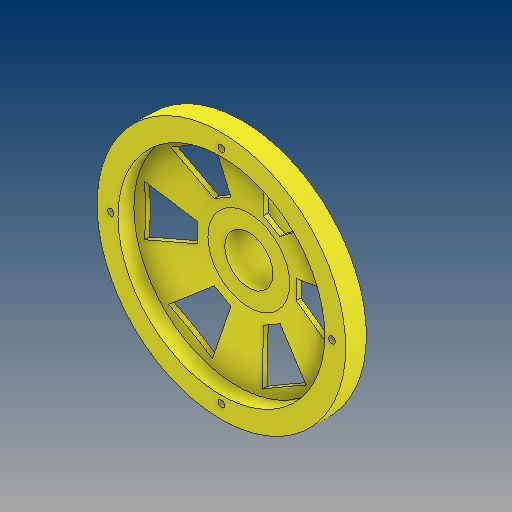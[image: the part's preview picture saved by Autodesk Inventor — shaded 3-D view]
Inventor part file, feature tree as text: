
AUTODESK INVENTOR PART (.ipt)
format: ipt  version: 2021 (Build 250183000, 183)  size: 367,616 bytes
history: native  units: in
note: dims shown in document units (in); Inventor stores cm internally (conversion verified against a paired STEP export)
features: sketch x10, thread x9, extrude x6, pattern_circular x5, revolve x4, plane x1
ambient origin geometry x8: Origin, YZ Plane, XZ Plane, XY Plane, X Axis, Y Axis, Z Axis, Center Point
bodies: Solid2 (feature_tree)
feature tree (35):
  plane  "Work Plane1"
  extrude  "Extrusion2"  Depth=3.0315in TaperAngle=0.0deg
  extrude  "Extrusion3"  Depth=3.937in
  revolve  "Revolution1"  Angle=90.0deg
  extrude  "Extrusion5"  Depth=2.3622in TaperAngle=360.0deg
  pattern_circular  "Circular Pattern2"  Count=14  [1 undecoded]
  extrude  "Extrusion9"  Depth=0.3937in TaperAngle=0.0deg
  extrude  "Extrusion10"  Depth=9.0551in
  pattern_circular  "Circular Pattern4"  Count=4 Angle=360.0deg
  sketch  "Sketch14"  dims[d43=0.9843in d44=0.0in d47=1.5748in d48=360.0deg d58=20.3543in d59=10.1772in d61=0.9843in d62=0.0in d63=0.9843in d64=0.0in]
  thread  "Thread5"  [1 undecoded]
  thread  "Thread6"  [1 undecoded]
  thread  "Thread7"  [1 undecoded]
  thread  "Thread8"  [1 undecoded]
  revolve  "Revolution4"  [1 undecoded]
  pattern_circular  "Circular Pattern5"  Count=4 Angle=360.0deg
  extrude  "Extrusion12"  Depth=0.3937in
  revolve  "Revolution5"  [1 undecoded]
  pattern_circular  "Circular Pattern6"  Angle=45.0deg  [1 undecoded]
  thread  "Thread9"  [1 undecoded]
  thread  "Thread10"  [1 undecoded]
  thread  "Thread11"  [1 undecoded]
  thread  "Thread12"  [1 undecoded]
  thread  "Thread13"  [1 undecoded]
  revolve  "Revolution6"  [1 undecoded]
  pattern_circular  "Circular Pattern7"  [2 undecoded]
  sketch  "Sketch5"  dims[d4=3.937in d5=3.0315in d6=0.0in]
  sketch  "Sketch6"  dims[d7=6.6929in d8=3.937in]
  sketch  "Sketch7"  dims[d9=0.3937in d10=0.0in d11=90.0deg]
  sketch  "Sketch9"  dims[d18=0.0in d19=0.0in d20=2.3622in d21=360.0deg d30=5.5118in]
  sketch  "Sketch11"  dims[d32=0.3937in d39=1.302in d40=0.0in]
  sketch  "Sketch12"  dims[d41=0.5512in d42=9.0551in]
  sketch  "Sketch16"  dims[d65=0.9843in d66=0.0in d67=0.9843in d68=0.0in]
  sketch  "Sketch17"  dims[d69=90.0deg d70=1.5748in d71=360.0deg]
  sketch  "Sketch18"  dims[d77=2.3228in d78=0.4724in d79=0.3937in d80=0.0in d82=45.0deg d83=45.0deg d84=90.0deg d85=1.9685in d86=360.0deg d88=0.3937in d89=0.0in d90=0.3937in d91=0.0in d92=0.3937in d93=0.0in d94=0.3937in d95=0.0in d96=0.3937in d97=0.0in d98=135.0deg d99=45.0deg d100=90.0deg d101=90.0deg d102=1.5748in d103=360.0deg d46=0.0344in]
note: 16 required parameter values undecoded (feature->parameter linkage not recoverable at this tier; creation-order binding heuristic only, values carry confidence <= 0.55)